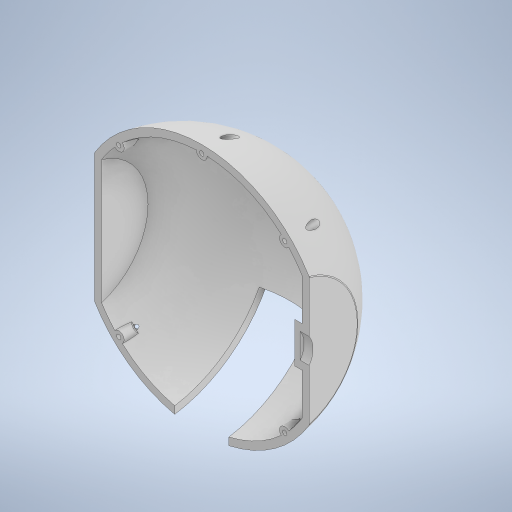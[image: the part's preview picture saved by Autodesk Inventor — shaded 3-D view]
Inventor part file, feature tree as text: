
AUTODESK INVENTOR PART (.ipt)
format: ipt  version: 2023 (Build 270158000, 158)  size: 488,960 bytes
history: native  units: mm
features: sketch x8, extrude x8, other x4, projected_geometry x2, revolve x1, shell x1, fillet x1, chamfer x1
ambient origin geometry x8: Origin, YZ Plane, XZ Plane, XY Plane, X Axis, Y Axis, Z Axis, Center Point
bodies: Body1 (feature_tree)
feature tree (26):
  other  "솔리드1"
  sketch  "스케치1"
  revolve  "회전1"
  other  "작업 평면2"
  extrude  "돌출14"  Depth=85.0mm
  shell  "쉘2"  Thickness=56.0mm
  extrude  "돌출15"  Depth=17.0mm
  other  "작업 평면3"
  fillet  "모깎기3"  Radius=140.0mm
  extrude  "돌출17"  Depth=4.0mm
  sketch  "스케치20"
  extrude  "돌출18"  TaperAngle=360.0deg  [1 undecoded]
  extrude  "돌출19"  [1 undecoded]
  extrude  "돌출20"  Depth=108.0mm TaperAngle=0.0deg
  other  "작업 평면4"
  sketch  "스케치24"
  chamfer  "모따기2"  Distance=4.0mm
  extrude  "돌출23"  Depth=2.5mm
  extrude  "돌출24"  Depth=80.0mm TaperAngle=360.0deg
  sketch  "스케치16"
  sketch  "스케치17"
  projected_geometry  "투영된 루프4"
  sketch  "스케치19"
  sketch  "스케치21"
  sketch  "스케치22"
  projected_geometry  "투영된 루프5"
note: 2 required parameter values undecoded (feature->parameter linkage not recoverable at this tier; creation-order binding heuristic only, values carry confidence <= 0.55)
